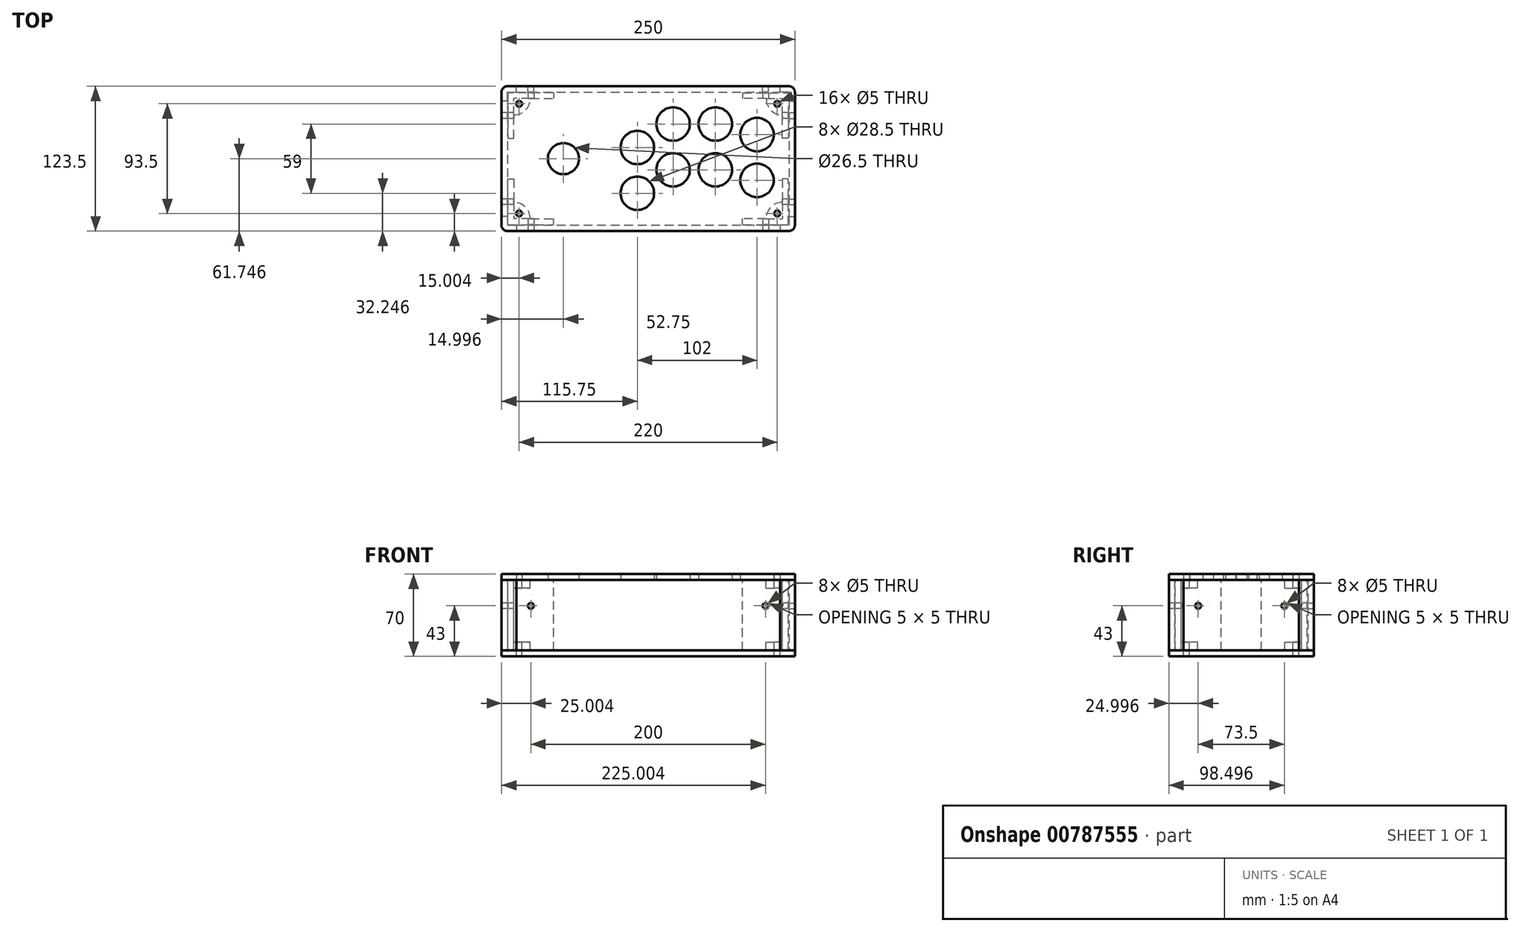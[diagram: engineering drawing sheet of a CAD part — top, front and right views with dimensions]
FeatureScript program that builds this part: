
annotation { "Feature Type Name" : "Feature", "Feature Type Description" : "" }
export const myFeature = defineFeature(function(context is Context, id is Id, definition is map)
    precondition{}
    {
        {
            var Q0;
            Q0=qCreatedBy(makeId("Top.planeOp"),FACE);
            var sketch = newSketch(context, id + "F0", { "sketchPlane" : qUnion([Q0])});
            skLineSegment(sketch, "E0.bottom", {"start": v(100, 54.6) * mm, "end": v(-100, 54.6) * mm, "construction": true});
            skLineSegment(sketch, "E0.top", {"start": v(100, -54.6) * mm, "end": v(-100, -54.6) * mm, "construction": true});
            skLineSegment(sketch, "E0.left", {"start": v(100, 54.6) * mm, "end": v(100, -54.6) * mm, "construction": true});
            skLineSegment(sketch, "E0.right", {"start": v(-100, 54.6) * mm, "end": v(-100, -54.6) * mm, "construction": true});
            skPoint(sketch, "E0.middle", {"position": v(0, 0) * mm});
            skLineSegment(sketch, "E1", {"start": v(-86.2, 54.6) * mm, "end": v(-86.2, 45.6) * mm, "construction": true});
            skLineSegment(sketch, "E2", {"start": v(-86.2, 45.6) * mm, "end": v(-86.2, 34.6) * mm, "construction": true});
            skLineSegment(sketch, "E3", {"start": v(-86.2, 34.6) * mm, "end": v(-86.2, 15.6) * mm, "construction": true});
            skLineSegment(sketch, "E4", {"start": v(-86.2, 15.6) * mm, "end": v(-86.2, 6.6) * mm, "construction": true});
            skLineSegment(sketch, "E5", {"start": v(-86.2, 6.6) * mm, "end": v(-86.2, -4.4) * mm, "construction": true});
            skLineSegment(sketch, "E6", {"start": v(-86.2, -4.4) * mm, "end": v(-86.2, -54.6) * mm, "construction": true});
            skLineSegment(sketch, "E7", {"start": v(-100, -44.04) * mm, "end": v(-5, -44.04) * mm, "construction": true});
            skLineSegment(sketch, "E8", {"start": v(-5, -44.04) * mm, "end": v(25.5, -44.04) * mm, "construction": true});
            skLineSegment(sketch, "E9", {"start": v(25.5, -44.04) * mm, "end": v(61.5, -44.04) * mm, "construction": true});
            skLineSegment(sketch, "E10", {"start": v(61.5, -44.04) * mm, "end": v(92, -44.04) * mm, "construction": true});
            skLineSegment(sketch, "E11", {"start": v(92, -44.04) * mm, "end": v(97, -44.04) * mm, "construction": true});
            skLineSegment(sketch, "E12", {"start": v(97, -44.04) * mm, "end": v(100, -44.04) * mm, "construction": true});
            skCircle(sketch, "E13", {"center": v(25.5, 54.6) * mm, "radius": 14.25 * mm});
            skCircle(sketch, "E14", {"center": v(61.5, 54.6) * mm, "radius": 14.25 * mm});
            skCircle(sketch, "E15", {"center": v(97, 45.6) * mm, "radius": 14.25 * mm});
            skCircle(sketch, "E16", {"center": v(-5, 34.6) * mm, "radius": 14.25 * mm});
            skCircle(sketch, "E17", {"center": v(-5, -4.4) * mm, "radius": 14.25 * mm});
            skCircle(sketch, "E18", {"center": v(25.5, 15.6) * mm, "radius": 14.25 * mm});
            skCircle(sketch, "E19", {"center": v(61.5, 15.6) * mm, "radius": 14.25 * mm});
            skCircle(sketch, "E20", {"center": v(97, 6.6) * mm, "radius": 14.25 * mm});
            skLineSegment(sketch, "E21", {"start": v(-5, -70.65) * mm, "end": v(-5, -44.04) * mm, "construction": true});
            skLineSegment(sketch, "E22", {"start": v(-5, -70.65) * mm, "end": v(-68, -70.65) * mm, "construction": true});
            skLineSegment(sketch, "E23", {"start": v(25.5, 54.6) * mm, "end": v(25.5, 68.85) * mm, "construction": true});
            skLineSegment(sketch, "E24", {"start": v(25.5, 68.85) * mm, "end": v(25.5, 86.85) * mm, "construction": true});
            skLineSegment(sketch, "E25", {"start": v(-5, -4.4) * mm, "end": v(-5, -18.65) * mm, "construction": true});
            skLineSegment(sketch, "E26", {"start": v(-5, -18.65) * mm, "end": v(-5, -36.65) * mm, "construction": true});
            skLineSegment(sketch, "E27", {"start": v(-68, 88.85) * mm, "end": v(25.5, 88.85) * mm, "construction": true});
            skLineSegment(sketch, "E28", {"start": v(-68, 88.85) * mm, "end": v(-68, 25.1) * mm, "construction": true});
            skLineSegment(sketch, "E29", {"start": v(-68, -38.65) * mm, "end": v(-68, 25.1) * mm, "construction": true});
            skCircle(sketch, "E30", {"center": v(-68, 25.1) * mm, "radius": 13.25 * mm});
            skLineSegment(sketch, "E31", {"start": v(25.5, 86.85) * mm, "end": v(25.5, 88.85) * mm, "construction": true});
            skLineSegment(sketch, "E32", {"start": v(-68, -38.65) * mm, "end": v(-5, -38.65) * mm, "construction": true});
            skLineSegment(sketch, "E33", {"start": v(-5, -38.65) * mm, "end": v(-5, -36.65) * mm, "construction": true});
            skLineSegment(sketch, "E34", {"start": v(-120.75, 86.85) * mm, "end": v(-120.75, -36.65) * mm});
            skLineSegment(sketch, "E35", {"start": v(129.25, -36.65) * mm, "end": v(129.25, 25.1) * mm});
            skLineSegment(sketch, "E36", {"start": v(-120.75, 86.85) * mm, "end": v(4.25, 86.85) * mm});
            skLineSegment(sketch, "E37", {"start": v(-120.75, -36.65) * mm, "end": v(129.25, -36.65) * mm});
            skCircle(sketch, "E38", {"center": v(-105.75, 71.85) * mm, "radius": 2.5 * mm});
            skLineSegment(sketch, "E39", {"start": v(-105.75, 71.85) * mm, "end": v(-120.75, 71.85) * mm, "construction": true});
            skLineSegment(sketch, "E40", {"start": v(-105.75, 71.85) * mm, "end": v(-105.75, 86.85) * mm, "construction": true});
            skLineSegment(sketch, "E41", {"start": v(4.25, 86.85) * mm, "end": v(129.25, 86.85) * mm});
            skLineSegment(sketch, "E42", {"start": v(4.25, 86.85) * mm, "end": v(4.25, 124.2) * mm, "construction": true});
            skCircle(sketch, "E43.MirrorC", {"center": v(114.25, 71.85) * mm, "radius": 2.5 * mm});
            skLineSegment(sketch, "E44", {"start": v(129.25, 25.1) * mm, "end": v(129.25, 86.85) * mm});
            skLineSegment(sketch, "E45", {"start": v(129.25, 25.1) * mm, "end": v(163.74, 25.1) * mm, "construction": true});
            skCircle(sketch, "E46.MirrorC", {"center": v(-105.75, -21.65) * mm, "radius": 2.5 * mm});
            skCircle(sketch, "E47.MirrorC", {"center": v(114.25, -21.65) * mm, "radius": 2.5 * mm});
            skSolve(sketch);
        }
        {
            var Q0;
            Q0=makeQuery(id+"F0.imprint","IMPRINT",FACE,{"disambiguationData":[TD([[makeQuery(id+"F0.imprint","IMPRINT",EDGE,{"derivedFrom":sQuery(id+"F0.wireOp",EDGE,"E13")}),-1.0]])]});
            extrude(context, id + "F1", {"entities" : qUnion([Q0]), "depth" : 5 * mm, "offsetDistance" : 25 * mm});
        }
        {
            var Q0;
            Q0=makeQuery(id+"F1.opExtrude","CAP_FACE",FACE,{"disambiguationData":[OSD([sQuery(id+"F0.wireOp",EDGE,"E13"),sQuery(id+"F0.wireOp",EDGE,"E14"),sQuery(id+"F0.wireOp",EDGE,"E15"),sQuery(id+"F0.wireOp",EDGE,"E16"),sQuery(id+"F0.wireOp",EDGE,"E17"),sQuery(id+"F0.wireOp",EDGE,"E18"),sQuery(id+"F0.wireOp",EDGE,"E19"),sQuery(id+"F0.wireOp",EDGE,"E20"),sQuery(id+"F0.wireOp",EDGE,"E30"),sQuery(id+"F0.wireOp",EDGE,"E34"),sQuery(id+"F0.wireOp",EDGE,"E35"),sQuery(id+"F0.wireOp",EDGE,"E36"),sQuery(id+"F0.wireOp",EDGE,"E37"),sQuery(id+"F0.wireOp",EDGE,"E38"),sQuery(id+"F0.wireOp",EDGE,"E41"),sQuery(id+"F0.wireOp",EDGE,"E43.MirrorC"),sQuery(id+"F0.wireOp",EDGE,"E44"),sQuery(id+"F0.wireOp",EDGE,"E46.MirrorC"),sQuery(id+"F0.wireOp",EDGE,"E47.MirrorC")])],"isStart":true});
            var sketch = newSketch(context, id + "F2", { "sketchPlane" : qUnion([Q0])});
            skLineSegment(sketch, "E48.bottom", {"start": v(-96.25, -81.35) * mm, "end": v(-115.25, -81.35) * mm});
            skLineSegment(sketch, "E48.top", {"start": v(-110.25, -62.35) * mm, "end": v(-110.25, -62.35) * mm});
            skLineSegment(sketch, "E48.left", {"start": v(-96.25, -76.35) * mm, "end": v(-96.25, -76.35) * mm});
            skLineSegment(sketch, "E48.right", {"start": v(-115.25, -81.35) * mm, "end": v(-115.25, -62.35) * mm});
            skPoint(sketch, "E48.middle", {"position": v(-105.75, -71.85) * mm});
            skCircle(sketch, "E49.0", {"center": v(-105.75, -71.85) * mm, "radius": 2.5 * mm});
            skLineSegment(sketch, "E50", {"start": v(-115.25, -62.35) * mm, "end": v(-115.25, -42.35) * mm});
            skLineSegment(sketch, "E51", {"start": v(-115.25, -42.35) * mm, "end": v(-110.25, -42.35) * mm});
            skLineSegment(sketch, "E52", {"start": v(-110.25, -42.35) * mm, "end": v(-110.25, -62.35) * mm});
            skLineSegment(sketch, "E53", {"start": v(-96.25, -81.35) * mm, "end": v(-76.25, -81.35) * mm});
            skLineSegment(sketch, "E54", {"start": v(-76.25, -81.35) * mm, "end": v(-76.25, -76.35) * mm});
            skLineSegment(sketch, "E55", {"start": v(-96.25, -76.35) * mm, "end": v(-76.25, -76.35) * mm});
            skArc(sketch, "E56", {"start": v(-96.25, -76.35) * mm, "mid": v(-100.35, -66.45) * mm, "end": v(-110.25, -62.35) * mm});
            skLineSegment(sketch, "E57", {"start": v(4.25, -86.85) * mm, "end": v(4.25, -125.73) * mm, "construction": true});
            skLineSegment(sketch, "E58", {"start": v(129.25, -25.1) * mm, "end": v(156.98, -25.1) * mm, "construction": true});
            skLineSegment(sketch, "E59.MirrorCS", {"start": v(84.75, -81.35) * mm, "end": v(84.75, -76.35) * mm});
            skLineSegment(sketch, "E60.MirrorCS", {"start": v(123.75, -42.35) * mm, "end": v(118.75, -42.35) * mm});
            skCircle(sketch, "E61.MirrorC", {"center": v(114.25, -71.85) * mm, "radius": 2.5 * mm});
            skLineSegment(sketch, "E62.MirrorCS", {"start": v(123.75, -81.35) * mm, "end": v(123.75, -62.35) * mm});
            skLineSegment(sketch, "E63.MirrorCS", {"start": v(104.75, -81.35) * mm, "end": v(123.75, -81.35) * mm});
            skLineSegment(sketch, "E64.MirrorCS", {"start": v(104.75, -76.35) * mm, "end": v(84.75, -76.35) * mm});
            skLineSegment(sketch, "E65.MirrorCS", {"start": v(123.75, -62.35) * mm, "end": v(123.75, -42.35) * mm});
            skLineSegment(sketch, "E66.MirrorCS", {"start": v(104.75, -81.35) * mm, "end": v(84.75, -81.35) * mm});
            skLineSegment(sketch, "E67.MirrorCS", {"start": v(118.75, -42.35) * mm, "end": v(118.75, -62.35) * mm});
            skArc(sketch, "E68.MirrorCS", {"start": v(104.75, -76.35) * mm, "mid": v(108.85, -66.45) * mm, "end": v(118.75, -62.35) * mm});
            skLineSegment(sketch, "E69.MirrorCS", {"start": v(123.75, -7.85) * mm, "end": v(118.75, -7.85) * mm});
            skLineSegment(sketch, "E70.MirrorCS", {"start": v(84.75, 31.15) * mm, "end": v(84.75, 26.15) * mm});
            skCircle(sketch, "E71.MirrorC", {"center": v(114.25, 21.65) * mm, "radius": 2.5 * mm});
            skLineSegment(sketch, "E72.MirrorCS", {"start": v(123.75, 31.15) * mm, "end": v(123.75, 12.15) * mm});
            skLineSegment(sketch, "E73.MirrorCS", {"start": v(118.75, -7.85) * mm, "end": v(118.75, 12.15) * mm});
            skLineSegment(sketch, "E74.MirrorCS", {"start": v(104.75, 31.15) * mm, "end": v(84.75, 31.15) * mm});
            skArc(sketch, "E75.MirrorCS", {"start": v(104.75, 26.15) * mm, "mid": v(108.85, 16.25) * mm, "end": v(118.75, 12.15) * mm});
            skLineSegment(sketch, "E76.MirrorCS", {"start": v(123.75, 12.15) * mm, "end": v(123.75, -7.85) * mm});
            skLineSegment(sketch, "E77.MirrorCS", {"start": v(104.75, 31.15) * mm, "end": v(123.75, 31.15) * mm});
            skLineSegment(sketch, "E78.MirrorCS", {"start": v(104.75, 26.15) * mm, "end": v(84.75, 26.15) * mm});
            skLineSegment(sketch, "E79.MirrorCS", {"start": v(-115.25, -7.85) * mm, "end": v(-110.25, -7.85) * mm});
            skLineSegment(sketch, "E80.MirrorCS", {"start": v(-76.25, 31.15) * mm, "end": v(-76.25, 26.15) * mm});
            skCircle(sketch, "E81.MirrorC", {"center": v(-105.75, 21.65) * mm, "radius": 2.5 * mm});
            skLineSegment(sketch, "E82.MirrorCS", {"start": v(-96.25, 26.15) * mm, "end": v(-76.25, 26.15) * mm});
            skLineSegment(sketch, "E83.MirrorCS", {"start": v(-96.25, 31.15) * mm, "end": v(-76.25, 31.15) * mm});
            skLineSegment(sketch, "E84.MirrorCS", {"start": v(-110.25, -7.85) * mm, "end": v(-110.25, 12.15) * mm});
            skLineSegment(sketch, "E85.MirrorCS", {"start": v(-115.25, 12.15) * mm, "end": v(-115.25, -7.85) * mm});
            skLineSegment(sketch, "E86.MirrorCS", {"start": v(-96.25, 31.15) * mm, "end": v(-115.25, 31.15) * mm});
            skLineSegment(sketch, "E87.MirrorCS", {"start": v(-115.25, 31.15) * mm, "end": v(-115.25, 12.15) * mm});
            skArc(sketch, "E88.MirrorCS", {"start": v(-96.25, 26.15) * mm, "mid": v(-100.35, 16.25) * mm, "end": v(-110.25, 12.15) * mm});
            skSolve(sketch);
        }
        {
            var Q0;
            Q0 = qSketchRegion(id + "F2", true);
            extrude(context, id + "F3", {"entities" : qUnion([Q0]), "depth" : 60 * mm, "offsetDistance" : 25 * mm});
        }
        {
            var Q0;
            Q0=makeQuery(id+"F3.opExtrude","CAP_FACE",FACE,{"disambiguationData":[OSD([sQuery(id+"F2.wireOp",EDGE,"E48.bottom"),sQuery(id+"F2.wireOp",EDGE,"E48.right"),sQuery(id+"F2.wireOp",EDGE,"E49.0"),sQuery(id+"F2.wireOp",EDGE,"E50"),sQuery(id+"F2.wireOp",EDGE,"E51"),sQuery(id+"F2.wireOp",EDGE,"E52"),sQuery(id+"F2.wireOp",EDGE,"E53"),sQuery(id+"F2.wireOp",EDGE,"E54"),sQuery(id+"F2.wireOp",EDGE,"E55"),sQuery(id+"F2.wireOp",EDGE,"E56")])],"isStart":true});
            var Q1;
            Q1=makeQuery(id+"F3.opExtrude","CAP_FACE",FACE,{"disambiguationData":[OSD([sQuery(id+"F2.wireOp",EDGE,"E48.bottom"),sQuery(id+"F2.wireOp",EDGE,"E48.right"),sQuery(id+"F2.wireOp",EDGE,"E49.0"),sQuery(id+"F2.wireOp",EDGE,"E50"),sQuery(id+"F2.wireOp",EDGE,"E51"),sQuery(id+"F2.wireOp",EDGE,"E52"),sQuery(id+"F2.wireOp",EDGE,"E53"),sQuery(id+"F2.wireOp",EDGE,"E54"),sQuery(id+"F2.wireOp",EDGE,"E55"),sQuery(id+"F2.wireOp",EDGE,"E56")])],"isStart":false});
            cPlane(context, id + "F4", {"entities" : qUnion([Q0, Q1]), "cplaneType" : CPlaneType.MID_PLANE, "offset" : 25 * mm, "width" : 150 * mm, "height" : 150 * mm});
        }
        {
            var Q0;
            Q0=qCreatedBy(id+"F4.planeOp",FACE);
            var sketch = newSketch(context, id + "F5", { "sketchPlane" : qUnion([Q0])});
            skLineSegment(sketch, "E89.bottom", {"start": v(-96.25, 62.35) * mm, "end": v(-110.25, 62.35) * mm});
            skLineSegment(sketch, "E89.top", {"start": v(-96.25, 76.35) * mm, "end": v(-110.25, 76.35) * mm});
            skLineSegment(sketch, "E89.left", {"start": v(-96.25, 62.35) * mm, "end": v(-96.25, 76.35) * mm});
            skLineSegment(sketch, "E89.right", {"start": v(-110.25, 62.35) * mm, "end": v(-110.25, 76.35) * mm});
            skPoint(sketch, "E89.middle", {"position": v(-103.25, 69.35) * mm});
            skLineSegment(sketch, "E90", {"start": v(-76.25, 81.35) * mm, "end": v(84.75, 81.35) * mm, "construction": true});
            skLineSegment(sketch, "E91", {"start": v(123.75, 42.35) * mm, "end": v(123.75, 7.85) * mm, "construction": true});
            skLineSegment(sketch, "E92", {"start": v(4.25, 81.35) * mm, "end": v(4.25, 25.1) * mm, "construction": true});
            skPoint(sketch, "E92.endSnap0", {"position": v(123.75, 25.1) * mm});
            skLineSegment(sketch, "E93", {"start": v(4.25, 25.1) * mm, "end": v(123.75, 25.1) * mm, "construction": true});
            skLineSegment(sketch, "E94.MirrorCS", {"start": v(104.75, 62.35) * mm, "end": v(118.75, 62.35) * mm});
            skPoint(sketch, "E95.MirrorP", {"position": v(111.75, 69.35) * mm});
            skLineSegment(sketch, "E96.MirrorCS", {"start": v(104.75, 76.35) * mm, "end": v(118.75, 76.35) * mm});
            skLineSegment(sketch, "E97.MirrorCS", {"start": v(118.75, 62.35) * mm, "end": v(118.75, 76.35) * mm});
            skLineSegment(sketch, "E98.MirrorCS", {"start": v(104.75, 62.35) * mm, "end": v(104.75, 76.35) * mm});
            skPoint(sketch, "E99.MirrorP", {"position": v(-103.25, -19.15) * mm});
            skLineSegment(sketch, "E100.MirrorCS", {"start": v(118.75, -12.15) * mm, "end": v(118.75, -26.15) * mm});
            skLineSegment(sketch, "E101.MirrorCS", {"start": v(104.75, -26.15) * mm, "end": v(118.75, -26.15) * mm});
            skLineSegment(sketch, "E102.MirrorCS", {"start": v(104.75, -12.15) * mm, "end": v(118.75, -12.15) * mm});
            skLineSegment(sketch, "E103.MirrorCS", {"start": v(-96.25, -26.15) * mm, "end": v(-110.25, -26.15) * mm});
            skLineSegment(sketch, "E104.MirrorCS", {"start": v(-110.25, -12.15) * mm, "end": v(-110.25, -26.15) * mm});
            skLineSegment(sketch, "E105.MirrorCS", {"start": v(-96.25, -12.15) * mm, "end": v(-96.25, -26.15) * mm});
            skLineSegment(sketch, "E106.MirrorCS", {"start": v(-96.25, -12.15) * mm, "end": v(-110.25, -12.15) * mm});
            skPoint(sketch, "E107.MirrorP", {"position": v(111.75, -19.15) * mm});
            skLineSegment(sketch, "E108.MirrorCS", {"start": v(104.75, -12.15) * mm, "end": v(104.75, -26.15) * mm});
            skSolve(sketch);
        }
        {
            var Q0;
            Q0 = qSketchRegion(id + "F5", true);
            extrude(context, id + "F6", {"entities" : qUnion([Q0]), "operationType" : NewBodyOperationType.REMOVE, "endBound" : BoundingType.SYMMETRIC, "oppositeDirection" : true, "depth" : 46 * mm, "offsetDistance" : 25 * mm});
        }
        {
            var Q0;
            Q0=makeQuery(id+"F3.opExtrude","SWEPT_FACE",FACE,{"disambiguationData":[OSD([sQuery(id+"F2.wireOp",EDGE,"E83.MirrorCS"),sQuery(id+"F2.wireOp",EDGE,"E86.MirrorCS")])]});
            var sketch = newSketch(context, id + "F7", { "sketchPlane" : qUnion([Q0])});
            skLineSegment(sketch, "E109", {"start": v(-95.75, 0) * mm, "end": v(-95.75, -22) * mm});
            skLineSegment(sketch, "E110", {"start": v(-95.75, -22) * mm, "end": v(-95.75, -60) * mm});
            skLineSegment(sketch, "E111", {"start": v(-76.25, 0) * mm, "end": v(84.75, 0) * mm, "construction": true});
            skLineSegment(sketch, "E112", {"start": v(4.25, 0) * mm, "end": v(4.25, 27.29) * mm, "construction": true});
            skCircle(sketch, "E113", {"center": v(-95.75, -22) * mm, "radius": 2.5 * mm});
            skCircle(sketch, "E114.MirrorC", {"center": v(104.25, -22) * mm, "radius": 2.5 * mm});
            skSolve(sketch);
        }
        {
            var Q0;
            Q0 = qSketchRegion(id + "F7", true);
            extrude(context, id + "F8", {"entities" : qUnion([Q0]), "operationType" : NewBodyOperationType.REMOVE, "endBound" : BoundingType.THROUGH_ALL, "oppositeDirection" : true, "depth" : 25 * mm, "offsetDistance" : 25 * mm});
        }
        {
            var Q0;
            Q0=makeQuery(id+"F3.opExtrude","SWEPT_FACE",FACE,{"disambiguationData":[OSD([sQuery(id+"F2.wireOp",EDGE,"E48.right"),sQuery(id+"F2.wireOp",EDGE,"E50")])]});
            var sketch = newSketch(context, id + "F9", { "sketchPlane" : qUnion([Q0])});
            skLineSegment(sketch, "E115", {"start": v(-42.35, 0) * mm, "end": v(-7.85, 0) * mm, "construction": true});
            skLineSegment(sketch, "E116", {"start": v(-25.1, 0) * mm, "end": v(-25.1, 13.41) * mm, "construction": true});
            skLineSegment(sketch, "E117", {"start": v(-61.85, 0) * mm, "end": v(-61.85, -22) * mm, "construction": true});
            skLineSegment(sketch, "E118", {"start": v(-61.85, -22) * mm, "end": v(-61.85, -60) * mm, "construction": true});
            skCircle(sketch, "E119", {"center": v(-61.85, -22) * mm, "radius": 2.5 * mm});
            skCircle(sketch, "E120.MirrorC", {"center": v(11.65, -22) * mm, "radius": 2.5 * mm});
            skSolve(sketch);
        }
        {
            var Q0;
            Q0 = qSketchRegion(id + "F9", true);
            extrude(context, id + "F10", {"entities" : qUnion([Q0]), "operationType" : NewBodyOperationType.REMOVE, "endBound" : BoundingType.THROUGH_ALL, "oppositeDirection" : true, "depth" : 25 * mm, "offsetDistance" : 25 * mm});
        }
        {
            var Q0;
            Q0=makeQuery(id+"F3.opExtrude","CAP_FACE",FACE,{"disambiguationData":[OSD([sQuery(id+"F2.wireOp",EDGE,"E79.MirrorCS"),sQuery(id+"F2.wireOp",EDGE,"E80.MirrorCS"),sQuery(id+"F2.wireOp",EDGE,"E81.MirrorC"),sQuery(id+"F2.wireOp",EDGE,"E82.MirrorCS"),sQuery(id+"F2.wireOp",EDGE,"E83.MirrorCS"),sQuery(id+"F2.wireOp",EDGE,"E84.MirrorCS"),sQuery(id+"F2.wireOp",EDGE,"E85.MirrorCS"),sQuery(id+"F2.wireOp",EDGE,"E86.MirrorCS"),sQuery(id+"F2.wireOp",EDGE,"E87.MirrorCS"),sQuery(id+"F2.wireOp",EDGE,"E88.MirrorCS")])],"isStart":false});
            var Q1;
            Q1=makeQuery(id+"F3.opExtrude","CAP_VERTEX",VERTEX,{"disambiguationData":[OSD([sQuery(id+"F2.wireOp",EDGE,"E86.MirrorCS"),sQuery(id+"F2.wireOp",EDGE,"E87.MirrorCS")])],"isStart":false});
            cPlane(context, id + "F11", {"entities" : qUnion([Q0, Q1]), "cplaneType" : CPlaneType.PLANE_POINT, "offset" : 25 * mm, "width" : 150 * mm, "height" : 150 * mm});
        }
        {
            var Q0;
            Q0=qCreatedBy(id+"F11.planeOp",FACE);
            var sketch = newSketch(context, id + "F12", { "sketchPlane" : qUnion([Q0])});
            skPoint(sketch, "E121", {"position": v(-120.75, 36.65) * mm});
            skPoint(sketch, "E122", {"position": v(-120.75, -86.85) * mm});
            skPoint(sketch, "E123", {"position": v(129.25, 36.65) * mm});
            skPoint(sketch, "E124", {"position": v(129.25, -86.85) * mm});
            skLineSegment(sketch, "E125.bottom", {"start": v(-120.75, 36.65) * mm, "end": v(129.25, 36.65) * mm});
            skLineSegment(sketch, "E125.top", {"start": v(-120.75, -86.85) * mm, "end": v(129.25, -86.85) * mm});
            skLineSegment(sketch, "E125.left", {"start": v(-120.75, 36.65) * mm, "end": v(-120.75, -86.85) * mm});
            skLineSegment(sketch, "E125.right", {"start": v(129.25, 36.65) * mm, "end": v(129.25, -86.85) * mm});
            skCircle(sketch, "E126.0", {"center": v(-105.75, 21.65) * mm, "radius": 2.5 * mm});
            skCircle(sketch, "E126.1", {"center": v(114.25, 21.65) * mm, "radius": 2.5 * mm});
            skCircle(sketch, "E126.2", {"center": v(114.25, -71.85) * mm, "radius": 2.5 * mm});
            skCircle(sketch, "E126.3", {"center": v(-105.75, -71.85) * mm, "radius": 2.5 * mm});
            skSolve(sketch);
        }
        {
            var Q0;
            Q0 = qSketchRegion(id + "F12", true);
            extrude(context, id + "F13", {"entities" : qUnion([Q0]), "depth" : 5 * mm, "offsetDistance" : 25 * mm});
        }
        {
            var Q0;
            Q0=makeQuery(id+"F1.opExtrude","CAP_VERTEX",VERTEX,{"disambiguationData":[OSD([sQuery(id+"F0.wireOp",EDGE,"E34"),sQuery(id+"F0.wireOp",EDGE,"E37")])],"isStart":false});
            var Q1;
            Q1=makeQuery(id+"F1.opExtrude","SWEPT_FACE",FACE,{"disambiguationData":[OSD([sQuery(id+"F0.wireOp",EDGE,"E37")])]});
            cPlane(context, id + "F14", {"entities" : qUnion([Q0, Q1]), "cplaneType" : CPlaneType.PLANE_POINT, "offset" : 25 * mm, "width" : 150 * mm, "height" : 150 * mm});
        }
        {
            var Q0;
            Q0=qCreatedBy(id+"F14.planeOp",FACE);
            var sketch = newSketch(context, id + "F15", { "sketchPlane" : qUnion([Q0])});
            skCircle(sketch, "E127.4", {"center": v(-95.75, -22) * mm, "radius": 2.5 * mm});
            skCircle(sketch, "E127.5", {"center": v(104.25, -22) * mm, "radius": 2.5 * mm});
            skLineSegment(sketch, "E128", {"start": v(-115.25, -30) * mm, "end": v(-108.25, -30) * mm, "construction": true});
            skLineSegment(sketch, "E129", {"start": v(-108.25, 0) * mm, "end": v(-108.25, -60) * mm});
            skLineSegment(sketch, "E130", {"start": v(116.75, 0) * mm, "end": v(116.75, -60) * mm});
            skLineSegment(sketch, "E131", {"start": v(-108.25, 0) * mm, "end": v(116.75, 0) * mm});
            skLineSegment(sketch, "E132", {"start": v(116.75, -60) * mm, "end": v(-108.25, -60) * mm});
            skSolve(sketch);
        }
        {
            var Q0;
            Q0 = qSketchRegion(id + "F15", true);
            extrude(context, id + "F16", {"entities" : qUnion([Q0]), "oppositeDirection" : true, "depth" : 5 * mm, "offsetDistance" : 25 * mm});
        }
        {
            var Q0;
            Q0=makeQuery(id+"F1.opExtrude","SWEPT_FACE",FACE,{"disambiguationData":[OSD([sQuery(id+"F0.wireOp",EDGE,"E37")])]});
            var Q1;
            Q1=makeQuery(id+"F1.opExtrude","SWEPT_FACE",FACE,{"disambiguationData":[OSD([sQuery(id+"F0.wireOp",EDGE,"E36"),sQuery(id+"F0.wireOp",EDGE,"E41")])]});
            cPlane(context, id + "F17", {"entities" : qUnion([Q0, Q1]), "cplaneType" : CPlaneType.MID_PLANE, "offset" : 25 * mm, "width" : 150 * mm, "height" : 150 * mm});
        }
        {
            var Q0;
            Q0=makeQuery(id+"F1.opExtrude","SWEPT_FACE",FACE,{"disambiguationData":[OSD([sQuery(id+"F0.wireOp",EDGE,"E34")])]});
            var Q1;
            Q1=makeQuery(id+"F1.opExtrude","SWEPT_FACE",FACE,{"disambiguationData":[OSD([sQuery(id+"F0.wireOp",EDGE,"E35"),sQuery(id+"F0.wireOp",EDGE,"E44")])]});
            cPlane(context, id + "F18", {"entities" : qUnion([Q0, Q1]), "cplaneType" : CPlaneType.MID_PLANE, "offset" : 25 * mm, "width" : 150 * mm, "height" : 150 * mm});
        }
        {
            var Q0;
            Q0=makeQuery(id+"F1.opExtrude","SWEPT_FACE",FACE,{"disambiguationData":[OSD([sQuery(id+"F0.wireOp",EDGE,"E34")])]});
            cPlane(context, id + "F19", {"entities" : qUnion([Q0]), "cplaneType" : CPlaneType.OFFSET, "offset" : 0 * mm, "width" : 150 * mm, "height" : 150 * mm});
        }
        {
            var Q0;
            Q0=qCreatedBy(id+"F19.planeOp",FACE);
            var sketch = newSketch(context, id + "F20", { "sketchPlane" : qUnion([Q0])});
            skLineSegment(sketch, "E133.0", {"start": v(-81.35, -60) * mm, "end": v(-81.35, 0) * mm});
            skLineSegment(sketch, "E133.1", {"start": v(-74.35, 0) * mm, "end": v(24.15, 0) * mm});
            skLineSegment(sketch, "E133.2", {"start": v(31.15, -60) * mm, "end": v(31.15, 0) * mm});
            skLineSegment(sketch, "E133.3", {"start": v(24.15, -60) * mm, "end": v(-74.35, -60) * mm});
            skPoint(sketch, "E134.orphan", {"position": v(-86.85, 0) * mm});
            skPoint(sketch, "E135.orphan", {"position": v(-86.85, -60) * mm});
            skPoint(sketch, "E136.orphan", {"position": v(36.65, -60) * mm});
            skPoint(sketch, "E137.orphan", {"position": v(36.65, 0) * mm});
            skCircle(sketch, "E138.0", {"center": v(11.65, -22) * mm, "radius": 2.5 * mm});
            skCircle(sketch, "E138.1", {"center": v(-61.85, -22) * mm, "radius": 2.5 * mm});
            skLineSegment(sketch, "E139", {"start": v(-81.35, -30) * mm, "end": v(-74.35, -30) * mm, "construction": true});
            skLineSegment(sketch, "E140", {"start": v(-74.35, 0) * mm, "end": v(-74.35, -60) * mm});
            skLineSegment(sketch, "E141", {"start": v(-25.1, 0) * mm, "end": v(-25.1, 38.68) * mm, "construction": true});
            skLineSegment(sketch, "E142.MirrorCS", {"start": v(24.15, 0) * mm, "end": v(24.15, -60) * mm});
            skSolve(sketch);
        }
        {
            var Q0;
            Q0 = qSketchRegion(id + "F20", true);
            extrude(context, id + "F21", {"entities" : qUnion([Q0]), "oppositeDirection" : true, "depth" : 5 * mm, "offsetDistance" : 25 * mm});
        }
        {
            var Q0;
            Q0=makeQuery(id+"F21.opExtrude","SWEPT_BODY",BODY,{"disambiguationData":[OSD([sQuery(id+"F20.wireOp",EDGE,"E133.0"),sQuery(id+"F20.wireOp",EDGE,"E133.1"),sQuery(id+"F20.wireOp",EDGE,"E133.2"),sQuery(id+"F20.wireOp",EDGE,"E133.3"),sQuery(id+"F20.wireOp",EDGE,"E138.0"),sQuery(id+"F20.wireOp",EDGE,"E138.1")])]});
            var Q1;
            Q1=qCreatedBy(id+"F18.planeOp",FACE);
            mirror(context, id + "F22", {"entities" : qUnion([Q0]), "mirrorPlane" : qUnion([Q1])});
        }
        {
            var Q0;
            Q0=makeQuery(id+"F13.opExtrude","CAP_FACE",FACE,{"disambiguationData":[OSD([sQuery(id+"F12.wireOp",EDGE,"E125.bottom"),sQuery(id+"F12.wireOp",EDGE,"E125.top"),sQuery(id+"F12.wireOp",EDGE,"E125.left"),sQuery(id+"F12.wireOp",EDGE,"E125.right"),sQuery(id+"F12.wireOp",EDGE,"E126.0"),sQuery(id+"F12.wireOp",EDGE,"E126.1"),sQuery(id+"F12.wireOp",EDGE,"E126.2"),sQuery(id+"F12.wireOp",EDGE,"E126.3")])],"isStart":true});
            cPlane(context, id + "F23", {"entities" : qUnion([Q0]), "cplaneType" : CPlaneType.OFFSET, "offset" : 0 * mm, "width" : 150 * mm, "height" : 150 * mm});
        }
        {
            var Q0;
            Q0=qCreatedBy(id+"F23.planeOp",FACE);
            var sketch = newSketch(context, id + "F24", { "sketchPlane" : qUnion([Q0])});
            skLineSegment(sketch, "E143.0", {"start": v(-115.75, -24.15) * mm, "end": v(-120.75, -24.15) * mm});
            skLineSegment(sketch, "E143.1", {"start": v(-120.75, -36.65) * mm, "end": v(-120.75, -24.15) * mm});
            skLineSegment(sketch, "E143.2", {"start": v(-120.75, -36.65) * mm, "end": v(-108.25, -36.65) * mm});
            skLineSegment(sketch, "E143.3", {"start": v(-108.25, -31.65) * mm, "end": v(-108.25, -36.65) * mm});
            skPoint(sketch, "E144.orphan", {"position": v(-120.75, 86.85) * mm});
            skPoint(sketch, "E145.orphan", {"position": v(129.25, -36.65) * mm});
            skLineSegment(sketch, "E146", {"start": v(-115.75, -24.15) * mm, "end": v(-115.75, -31.65) * mm});
            skLineSegment(sketch, "E147", {"start": v(-115.75, -31.65) * mm, "end": v(-108.25, -31.65) * mm});
            skSolve(sketch);
        }
        {
            var Q0;
            Q0 = qSketchRegion(id + "F24", true);
            extrude(context, id + "F25", {"entities" : qUnion([Q0]), "depth" : 60 * mm, "offsetDistance" : 25 * mm});
        }
        {
            var Q0;
            Q0=makeQuery(id+"F25.opExtrude","SWEPT_BODY",BODY,{"disambiguationData":[OSD([sQuery(id+"F24.wireOp",EDGE,"E143.0"),sQuery(id+"F24.wireOp",EDGE,"E143.1"),sQuery(id+"F24.wireOp",EDGE,"E143.2"),sQuery(id+"F24.wireOp",EDGE,"E143.3"),sQuery(id+"F24.wireOp",EDGE,"E146"),sQuery(id+"F24.wireOp",EDGE,"E147")])]});
            var Q1;
            Q1=qCreatedBy(id+"F18.planeOp",FACE);
            mirror(context, id + "F26", {"entities" : qUnion([Q0]), "mirrorPlane" : qUnion([Q1])});
        }
        {
            var Q0;
            Q0=makeQuery(id+"F16.opExtrude","SWEPT_BODY",BODY,{"disambiguationData":[OSD([sQuery(id+"F15.wireOp",EDGE,"E127.4"),sQuery(id+"F15.wireOp",EDGE,"E127.5"),sQuery(id+"F15.wireOp",EDGE,"E129"),sQuery(id+"F15.wireOp",EDGE,"E130"),sQuery(id+"F15.wireOp",EDGE,"E131"),sQuery(id+"F15.wireOp",EDGE,"E132")])]});
            var Q1;
            Q1=makeQuery(id+"F26.opPattern","COPY",BODY,{"derivedFrom":makeQuery(id+"F25.opExtrude","SWEPT_BODY",BODY,{"disambiguationData":[OSD([sQuery(id+"F24.wireOp",EDGE,"E143.0"),sQuery(id+"F24.wireOp",EDGE,"E143.1"),sQuery(id+"F24.wireOp",EDGE,"E143.2"),sQuery(id+"F24.wireOp",EDGE,"E143.3"),sQuery(id+"F24.wireOp",EDGE,"E146"),sQuery(id+"F24.wireOp",EDGE,"E147")])]}),"instanceName":"1"});
            var Q2;
            Q2=makeQuery(id+"F25.opExtrude","SWEPT_BODY",BODY,{"disambiguationData":[OSD([sQuery(id+"F24.wireOp",EDGE,"E143.0"),sQuery(id+"F24.wireOp",EDGE,"E143.1"),sQuery(id+"F24.wireOp",EDGE,"E143.2"),sQuery(id+"F24.wireOp",EDGE,"E143.3"),sQuery(id+"F24.wireOp",EDGE,"E146"),sQuery(id+"F24.wireOp",EDGE,"E147")])]});
            var Q3;
            Q3=qCreatedBy(id+"F17.planeOp",FACE);
            mirror(context, id + "F27", {"entities" : qUnion([Q0, Q1, Q2]), "mirrorPlane" : qUnion([Q3])});
        }
        {
            var Q0;
            Q0=makeQuery(id+"F1.opExtrude","SWEPT_EDGE",EDGE,{"disambiguationData":[OSD([sQuery(id+"F0.wireOp",EDGE,"E34"),sQuery(id+"F0.wireOp",EDGE,"E37")])]});
            var Q1;
            Q1=makeQuery(id+"F25.opExtrude","SWEPT_EDGE",EDGE,{"disambiguationData":[OSD([sQuery(id+"F24.wireOp",EDGE,"E143.1"),sQuery(id+"F24.wireOp",EDGE,"E143.2")])]});
            var Q2;
            Q2=makeQuery(id+"F13.opExtrude","SWEPT_EDGE",EDGE,{"disambiguationData":[OSD([sQuery(id+"F12.wireOp",EDGE,"E125.bottom"),sQuery(id+"F12.wireOp",EDGE,"E125.left")])]});
            var Q3;
            Q3=makeQuery(id+"F1.opExtrude","SWEPT_EDGE",EDGE,{"disambiguationData":[OSD([sQuery(id+"F0.wireOp",EDGE,"E35"),sQuery(id+"F0.wireOp",EDGE,"E37")])]});
            var Q4;
            Q4=makeQuery(id+"F26.opPattern","COPY",EDGE,{"derivedFrom":makeQuery(id+"F25.opExtrude","SWEPT_EDGE",EDGE,{"disambiguationData":[OSD([sQuery(id+"F24.wireOp",EDGE,"E143.1"),sQuery(id+"F24.wireOp",EDGE,"E143.2")])]}),"instanceName":"1"});
            var Q5;
            Q5=makeQuery(id+"F13.opExtrude","SWEPT_EDGE",EDGE,{"disambiguationData":[OSD([sQuery(id+"F12.wireOp",EDGE,"E125.bottom"),sQuery(id+"F12.wireOp",EDGE,"E125.right")])]});
            var Q6;
            Q6=makeQuery(id+"F1.opExtrude","SWEPT_EDGE",EDGE,{"disambiguationData":[OSD([sQuery(id+"F0.wireOp",EDGE,"E41"),sQuery(id+"F0.wireOp",EDGE,"E44")])]});
            var Q7;
            Q7=makeQuery(id+"F27.opPattern","COPY",EDGE,{"derivedFrom":makeQuery(id+"F26.opPattern","COPY",EDGE,{"derivedFrom":makeQuery(id+"F25.opExtrude","SWEPT_EDGE",EDGE,{"disambiguationData":[OSD([sQuery(id+"F24.wireOp",EDGE,"E143.1"),sQuery(id+"F24.wireOp",EDGE,"E143.2")])]}),"instanceName":"1"}),"instanceName":"1"});
            var Q8;
            Q8=makeQuery(id+"F13.opExtrude","SWEPT_EDGE",EDGE,{"disambiguationData":[OSD([sQuery(id+"F12.wireOp",EDGE,"E125.top"),sQuery(id+"F12.wireOp",EDGE,"E125.right")])]});
            var Q9;
            Q9=makeQuery(id+"F1.opExtrude","SWEPT_EDGE",EDGE,{"disambiguationData":[OSD([sQuery(id+"F0.wireOp",EDGE,"E34"),sQuery(id+"F0.wireOp",EDGE,"E36")])]});
            var Q10;
            Q10=makeQuery(id+"F27.opPattern","COPY",EDGE,{"derivedFrom":makeQuery(id+"F25.opExtrude","SWEPT_EDGE",EDGE,{"disambiguationData":[OSD([sQuery(id+"F24.wireOp",EDGE,"E143.1"),sQuery(id+"F24.wireOp",EDGE,"E143.2")])]}),"instanceName":"1"});
            var Q11;
            Q11=makeQuery(id+"F13.opExtrude","SWEPT_EDGE",EDGE,{"disambiguationData":[OSD([sQuery(id+"F12.wireOp",EDGE,"E125.top"),sQuery(id+"F12.wireOp",EDGE,"E125.left")])]});
            fillet(context, id + "F28", {"entities" : qUnion([Q0, Q1, Q2, Q3, Q4, Q5, Q6, Q7, Q8, Q9, Q10, Q11]), "radius" : 5 * mm, "tangentPropagation" : true, "allowEdgeOverflow" : false});
        }
    });
